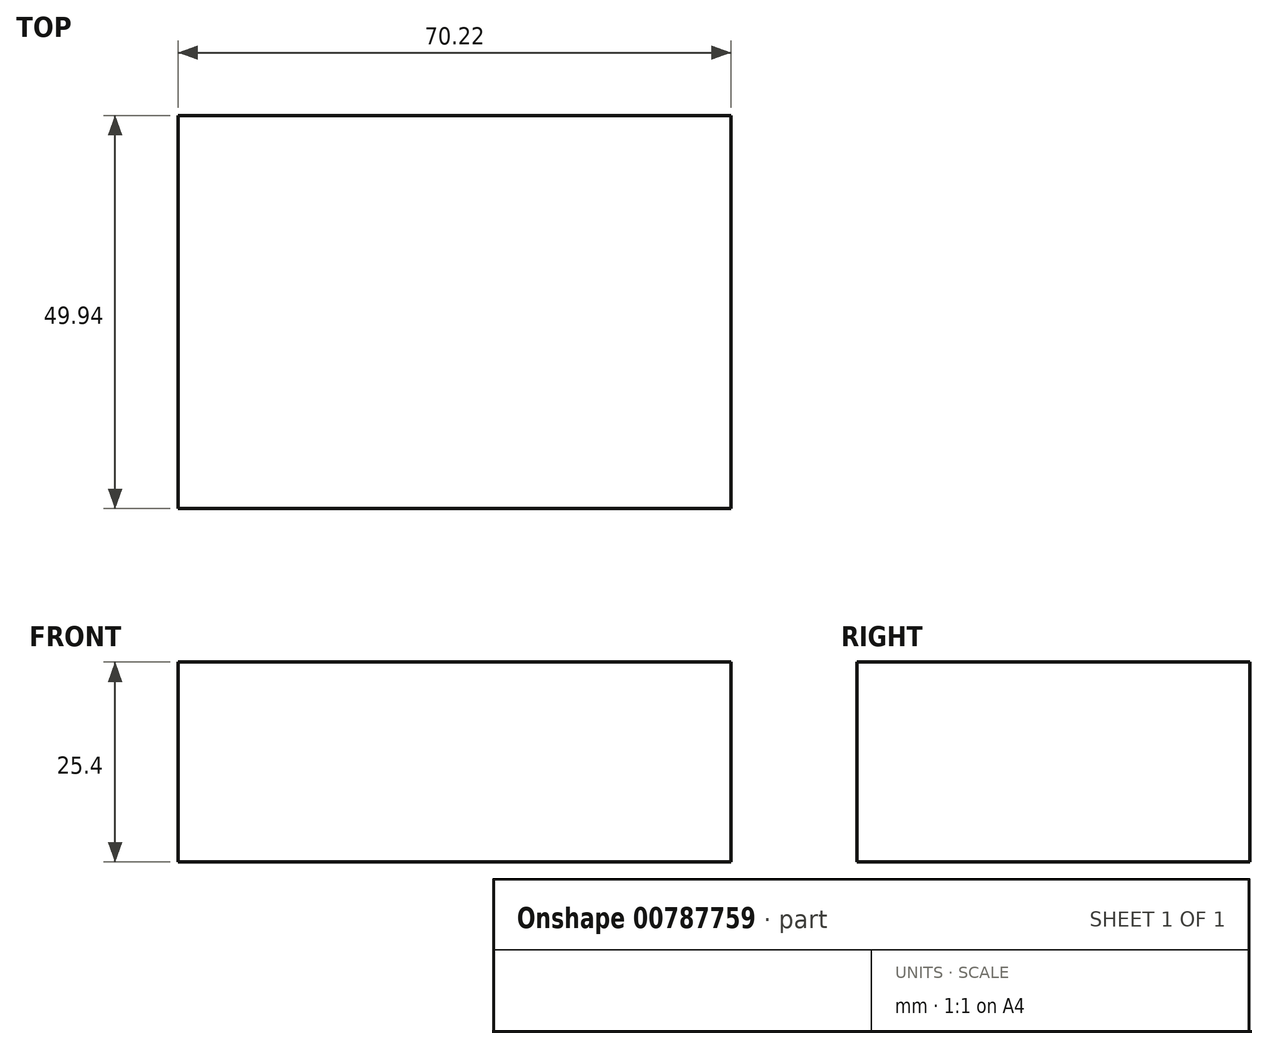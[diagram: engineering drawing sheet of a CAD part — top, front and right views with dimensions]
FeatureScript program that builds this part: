
annotation { "Feature Type Name" : "Feature", "Feature Type Description" : "" }
export const myFeature = defineFeature(function(context is Context, id is Id, definition is map)
    precondition{}
    {
        {
            var Q0;
            Q0=qCreatedBy(makeId("Top.planeOp"),FACE);
            var sketch = newSketch(context, id + "F0", { "sketchPlane" : qUnion([Q0])});
            skLineSegment(sketch, "E0", {"start": v(0, 0) * mm, "end": v(0, 49.94) * mm});
            skLineSegment(sketch, "E1", {"start": v(0, 0) * mm, "end": v(36.23, 0) * mm});
            skLineSegment(sketch, "E2", {"start": v(0, 0) * mm, "end": v(-34, 0) * mm});
            skLineSegment(sketch, "E3", {"start": v(-34, 0) * mm, "end": v(-34, 49.94) * mm});
            skLineSegment(sketch, "E4", {"start": v(-34, 49.94) * mm, "end": v(0, 49.94) * mm});
            skLineSegment(sketch, "E5", {"start": v(36.23, 49.94) * mm, "end": v(36.23, 0) * mm});
            skLineSegment(sketch, "E6", {"start": v(36.23, 49.94) * mm, "end": v(0, 49.94) * mm});
            skSolve(sketch);
        }
        {
            var Q0;
            Q0 = qSketchRegion(id + "F0", true);
            extrude(context, id + "F1", {"entities" : qUnion([Q0]), "depth" : 25.4 * mm, "offsetDistance" : 25.4 * mm});
        }
    });
